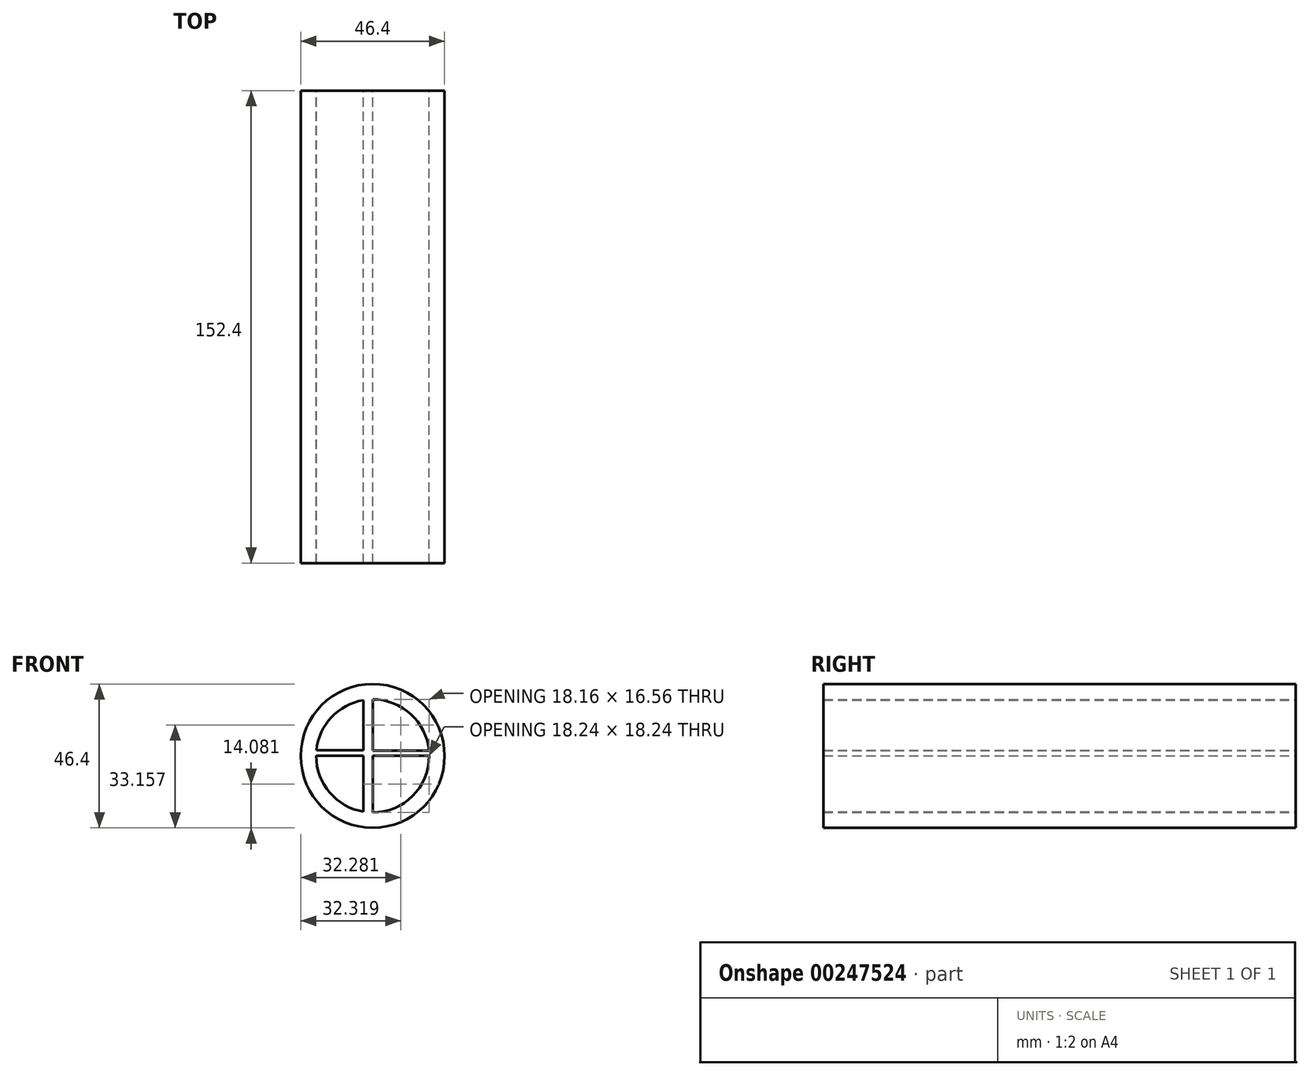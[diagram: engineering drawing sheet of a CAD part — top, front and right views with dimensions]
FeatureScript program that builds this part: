
annotation { "Feature Type Name" : "Feature", "Feature Type Description" : "" }
export const myFeature = defineFeature(function(context is Context, id is Id, definition is map)
    precondition{}
    {
        {
            var Q0;
            Q0=qCreatedBy(makeId("Front.planeOp"),FACE);
            var sketch = newSketch(context, id + "F0", { "sketchPlane" : qUnion([Q0])});
            skCircle(sketch, "E0", {"center": v(0, 0) * mm, "radius": 23.2 * mm});
            skArc(sketch, "E1", {"start": v(-18.24, 0) * mm, "mid": v(-13.9, -11.8) * mm, "end": v(-2.96, -18) * mm});
            skLineSegment(sketch, "E2.left", {"start": v(0, 18.24) * mm, "end": v(0, 1.68) * mm});
            skLineSegment(sketch, "E2.right", {"start": v(-2.96, 18) * mm, "end": v(-2.96, 1.84) * mm});
            skLineSegment(sketch, "E3.left", {"start": v(0, -18.24) * mm, "end": v(0, 0) * mm});
            skLineSegment(sketch, "E3.right", {"start": v(-2.96, -18) * mm, "end": v(-2.96, 0) * mm});
            skLineSegment(sketch, "E4.bottom", {"start": v(-2.96, 0) * mm, "end": v(-18.24, 0) * mm});
            skLineSegment(sketch, "E4.top", {"start": v(-2.96, 1.84) * mm, "end": v(-18.15, 1.84) * mm});
            skLineSegment(sketch, "E5.bottom", {"start": v(0, 0) * mm, "end": v(0, 0) * mm});
            skLineSegment(sketch, "E5.top", {"start": v(0, 3.56) * mm, "end": v(0, 3.56) * mm});
            skLineSegment(sketch, "E5.left", {"start": v(0, 1.68) * mm, "end": v(0, 3.56) * mm});
            skLineSegment(sketch, "E5.right", {"start": v(0, 1.68) * mm, "end": v(0, 3.56) * mm});
            skLineSegment(sketch, "E6.bottom", {"start": v(0, 0) * mm, "end": v(18.24, 0) * mm});
            skLineSegment(sketch, "E6.top", {"start": v(0, 1.68) * mm, "end": v(18.16, 1.68) * mm});
            skArc(sketch, "E7.trimOffspring", {"start": v(0, -18.24) * mm, "mid": v(12.9, -12.9) * mm, "end": v(18.24, 0) * mm});
            skArc(sketch, "E8.trimOffspring", {"start": v(18.16, 1.68) * mm, "mid": v(12.29, 13.48) * mm, "end": v(0, 18.24) * mm});
            skArc(sketch, "E9.trimOffspring", {"start": v(-2.96, 18) * mm, "mid": v(-13.3, 12.49) * mm, "end": v(-18.15, 1.84) * mm});
            skSolve(sketch);
        }
        {
            var Q0;
            Q0 = qSketchRegion(id + "F0", true);
            extrude(context, id + "F1", {"entities" : qUnion([Q0]), "depth" : 152.4 * mm});
        }
    });
